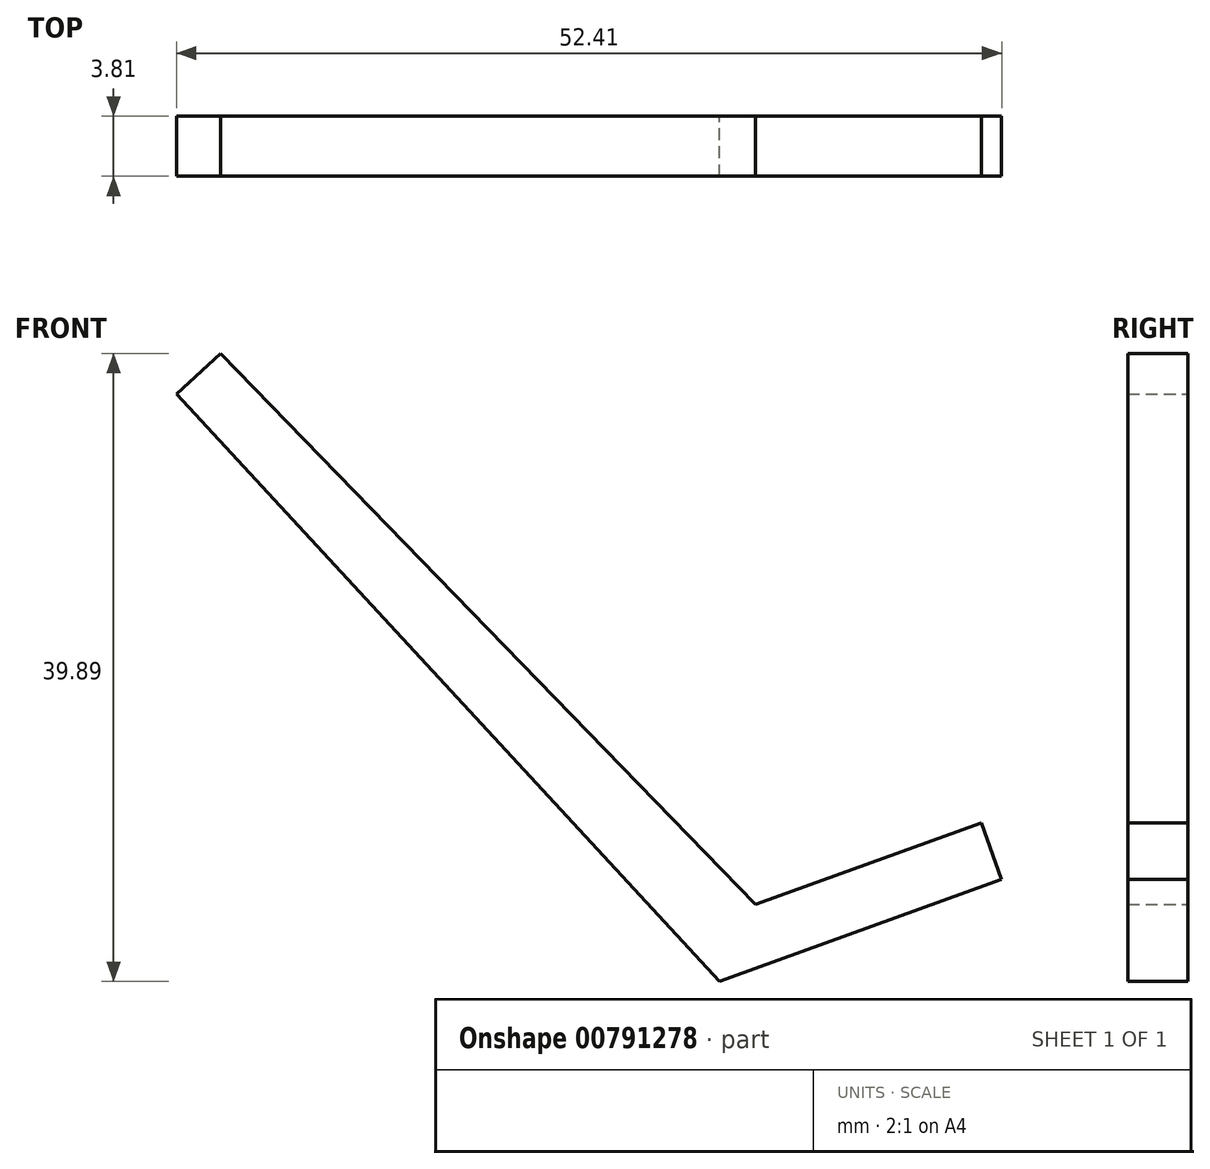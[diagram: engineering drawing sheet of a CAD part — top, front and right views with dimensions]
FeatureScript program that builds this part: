
annotation { "Feature Type Name" : "Feature", "Feature Type Description" : "" }
export const myFeature = defineFeature(function(context is Context, id is Id, definition is map)
    precondition{}
    {
        {
            var Q0;
            Q0=qCreatedBy(makeId("Front.planeOp"),FACE);
            var sketch = newSketch(context, id + "F0", { "sketchPlane" : qUnion([Q0])});
            skLineSegment(sketch, "E0", {"start": v(-34.65, 27.24) * mm, "end": v(-0.16, -10.06) * mm});
            skLineSegment(sketch, "E1", {"start": v(-0.16, -10.06) * mm, "end": v(17.76, -3.58) * mm});
            skLineSegment(sketch, "E2", {"start": v(-34.65, 27.24) * mm, "end": v(-31.85, 29.83) * mm});
            skLineSegment(sketch, "E3", {"start": v(17.76, -3.58) * mm, "end": v(16.46, 0) * mm});
            skLineSegment(sketch, "E4", {"start": v(16.46, 0) * mm, "end": v(2.13, -5.18) * mm});
            skLineSegment(sketch, "E5", {"start": v(2.13, -5.18) * mm, "end": v(-31.85, 29.83) * mm});
            skSolve(sketch);
        }
        {
            var Q0;
            Q0=makeQuery(id+"F0.imprint","IMPRINT",FACE,{"disambiguationData":[TD([[makeQuery(id+"F0.imprint","IMPRINT",EDGE,{"derivedFrom":sQuery(id+"F0.wireOp",EDGE,"E0")}),1.0]])]});
            extrude(context, id + "F1", {"entities" : qUnion([Q0]), "depth" : 3.8 * mm, "offsetDistance" : 25.4 * mm});
        }
    });
